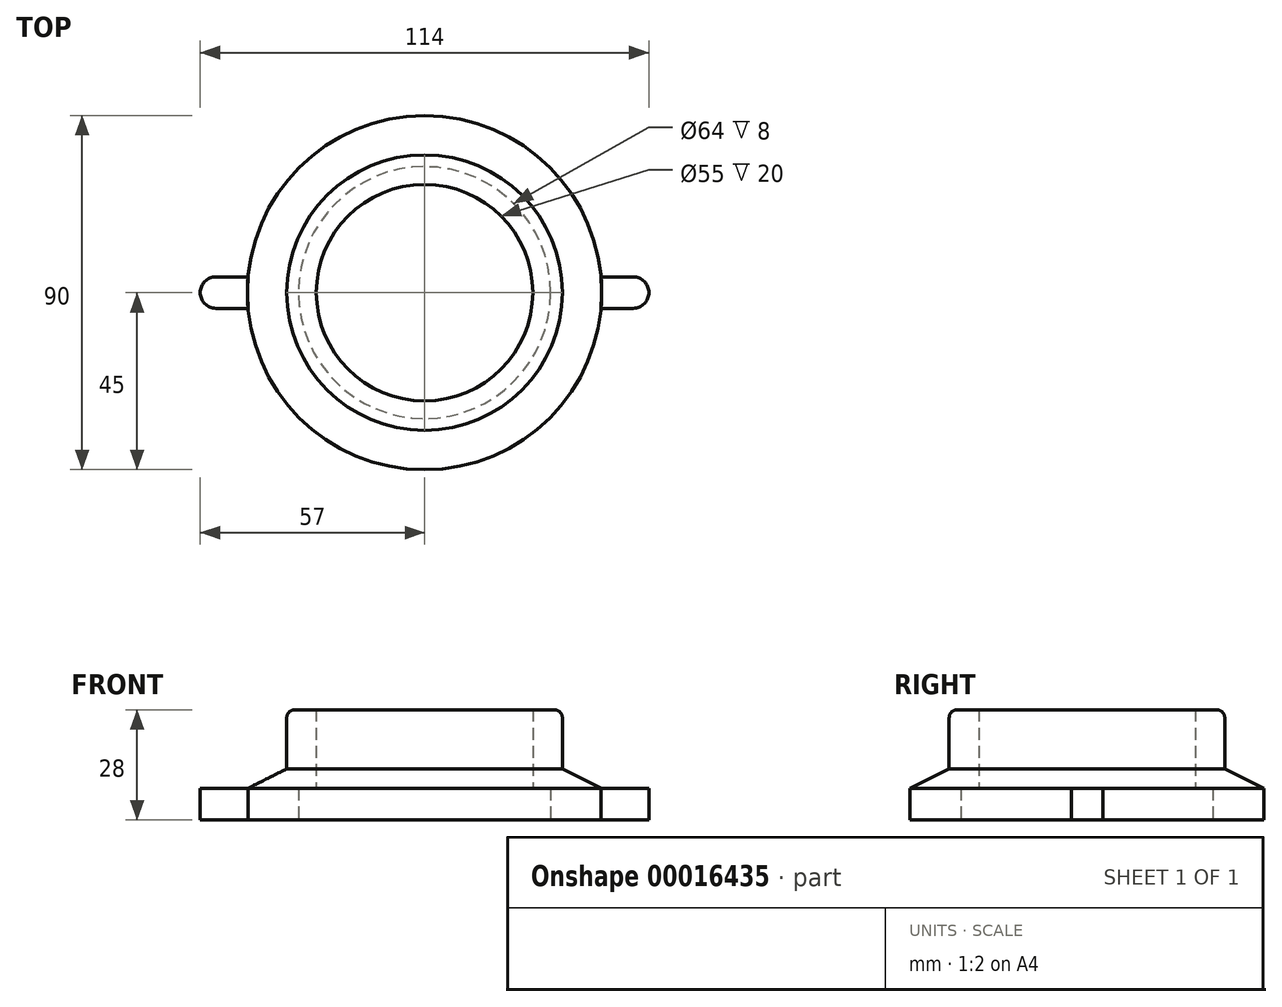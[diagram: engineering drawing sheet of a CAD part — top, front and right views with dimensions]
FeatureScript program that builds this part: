
annotation { "Feature Type Name" : "Feature", "Feature Type Description" : "" }
export const myFeature = defineFeature(function(context is Context, id is Id, definition is map)
    precondition{}
    {
        {
            var Q0;
            Q0=qCreatedBy(makeId("Right.planeOp"),FACE);
            var sketch = newSketch(context, id + "F0", { "sketchPlane" : qUnion([Q0])});
            skLineSegment(sketch, "E0", {"start": v(-45, 0) * mm, "end": v(-45, 8) * mm});
            skLineSegment(sketch, "E1", {"start": v(-45, 8) * mm, "end": v(-35, 13) * mm});
            skLineSegment(sketch, "E2", {"start": v(-35, 13) * mm, "end": v(-35, 28) * mm});
            skLineSegment(sketch, "E3", {"start": v(-35, 28) * mm, "end": v(-27.5, 28) * mm});
            skLineSegment(sketch, "E4", {"start": v(-27.5, 28) * mm, "end": v(-27.5, 8) * mm});
            skLineSegment(sketch, "E5", {"start": v(-27.5, 8) * mm, "end": v(-32, 8) * mm});
            skLineSegment(sketch, "E6", {"start": v(-32, 8) * mm, "end": v(-32, 0) * mm});
            skLineSegment(sketch, "E7", {"start": v(-32, 0) * mm, "end": v(-45, 0) * mm});
            skLineSegment(sketch, "E8", {"start": v(0, 0) * mm, "end": v(0, 43.63) * mm, "construction": true});
            skSolve(sketch);
        }
        {
            var Q0;
            Q0=makeQuery(id+"F0.imprint","IMPRINT",FACE,{"disambiguationData":[TD([[makeQuery(id+"F0.imprint","IMPRINT",EDGE,{"derivedFrom":sQuery(id+"F0.wireOp",EDGE,"E0")}),-1.0]])]});
            var Q1;
            Q1=sQuery(id+"F0.wireOp",EDGE,"E8");
            revolve(context, id + "F1", {"entities" : qUnion([Q0]), "axis" : qUnion([Q1]), "revolveType" : RevolveType.FULL});
        }
        {
            var Q0;
            Q0=makeQuery(id+"F1.opRevolve","SWEPT_FACE",FACE,{"disambiguationData":[OSD([sQuery(id+"F0.wireOp",EDGE,"E7")])]});
            var sketch = newSketch(context, id + "F2", { "sketchPlane" : qUnion([Q0])});
            skLineSegment(sketch, "E9.bottom", {"start": v(-53, 4) * mm, "end": v(-44.82, 4) * mm});
            skLineSegment(sketch, "E9.top", {"start": v(-53, -4) * mm, "end": v(-44.82, -4) * mm});
            skArc(sketch, "E10", {"start": v(-53, 4) * mm, "mid": v(-57, 0) * mm, "end": v(-53, -4) * mm});
            skArc(sketch, "E11.0", {"start": v(-44.82, 4) * mm, "mid": v(-45, 0) * mm, "end": v(-44.82, -4) * mm});
            skLineSegment(sketch, "E12", {"start": v(0, -64.74) * mm, "end": v(0, 82.92) * mm, "construction": true});
            skLineSegment(sketch, "E13.MirrorCS", {"start": v(53, -4) * mm, "end": v(44.82, -4) * mm});
            skLineSegment(sketch, "E14.MirrorCS", {"start": v(53, 4) * mm, "end": v(44.82, 4) * mm});
            skArc(sketch, "E15.MirrorCS", {"start": v(44.82, 4) * mm, "mid": v(45, 0) * mm, "end": v(44.82, -4) * mm});
            skArc(sketch, "E16.MirrorCS", {"start": v(53, 4) * mm, "mid": v(57, 0) * mm, "end": v(53, -4) * mm});
            skSolve(sketch);
        }
        {
            var Q0;
            Q0 = qSketchRegion(id + "F2", true);
            extrude(context, id + "F3", {"entities" : qUnion([Q0]), "oppositeDirection" : true, "depth" : 8 * mm});
        }
        {
            var Q0;
            Q0=makeQuery(id+"F1.opRevolve","SWEPT_EDGE",EDGE,{"disambiguationData":[OSD([sQuery(id+"F0.wireOp",EDGE,"E2"),sQuery(id+"F0.wireOp",EDGE,"E3")])]});
            fillet(context, id + "F4", {"entities" : qUnion([Q0]), "radius" : 2 * mm, "tangentPropagation" : true, "allowEdgeOverflow" : false});
        }
    });
